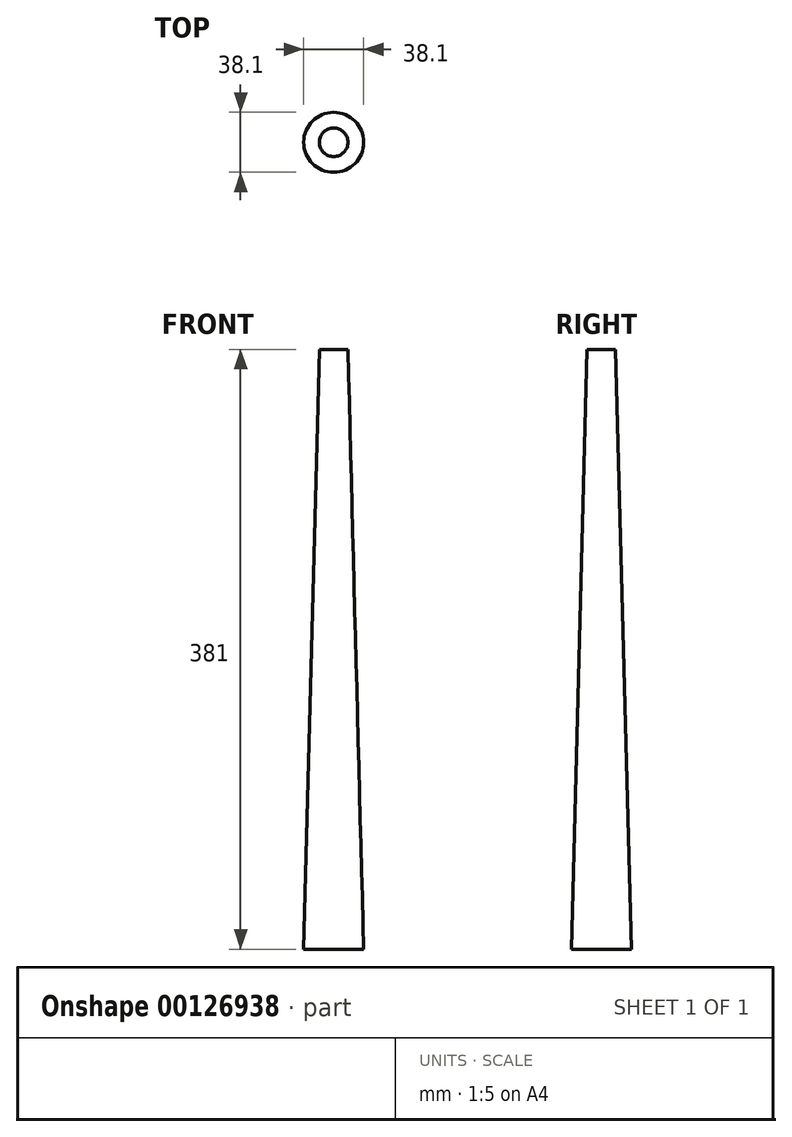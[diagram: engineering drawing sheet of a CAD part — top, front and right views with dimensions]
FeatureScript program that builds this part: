
annotation { "Feature Type Name" : "Feature", "Feature Type Description" : "" }
export const myFeature = defineFeature(function(context is Context, id is Id, definition is map)
    precondition{}
    {
        {
            var Q0;
            Q0=qCreatedBy(makeId("Top.planeOp"),FACE);
            var sketch = newSketch(context, id + "F0", { "sketchPlane" : qUnion([Q0])});
            skCircle(sketch, "E0", {"center": v(0, 0) * mm, "radius": 19.05 * mm});
            skSolve(sketch);
        }
        {
            var Q0;
            Q0=makeQuery(id+"F0.imprint","IMPRINT",FACE,{"disambiguationData":[TD([[makeQuery(id+"F0.imprint","IMPRINT",EDGE,{"derivedFrom":sQuery(id+"F0.wireOp",EDGE,"E0")}),1.0]])]});
            extrude(context, id + "F1", {"entities" : qUnion([Q0]), "depth" : 381 * mm, "hasDraft" : true, "draftAngle" : 1.5 * degree, "draftPullDirection" : true});
        }
    });
